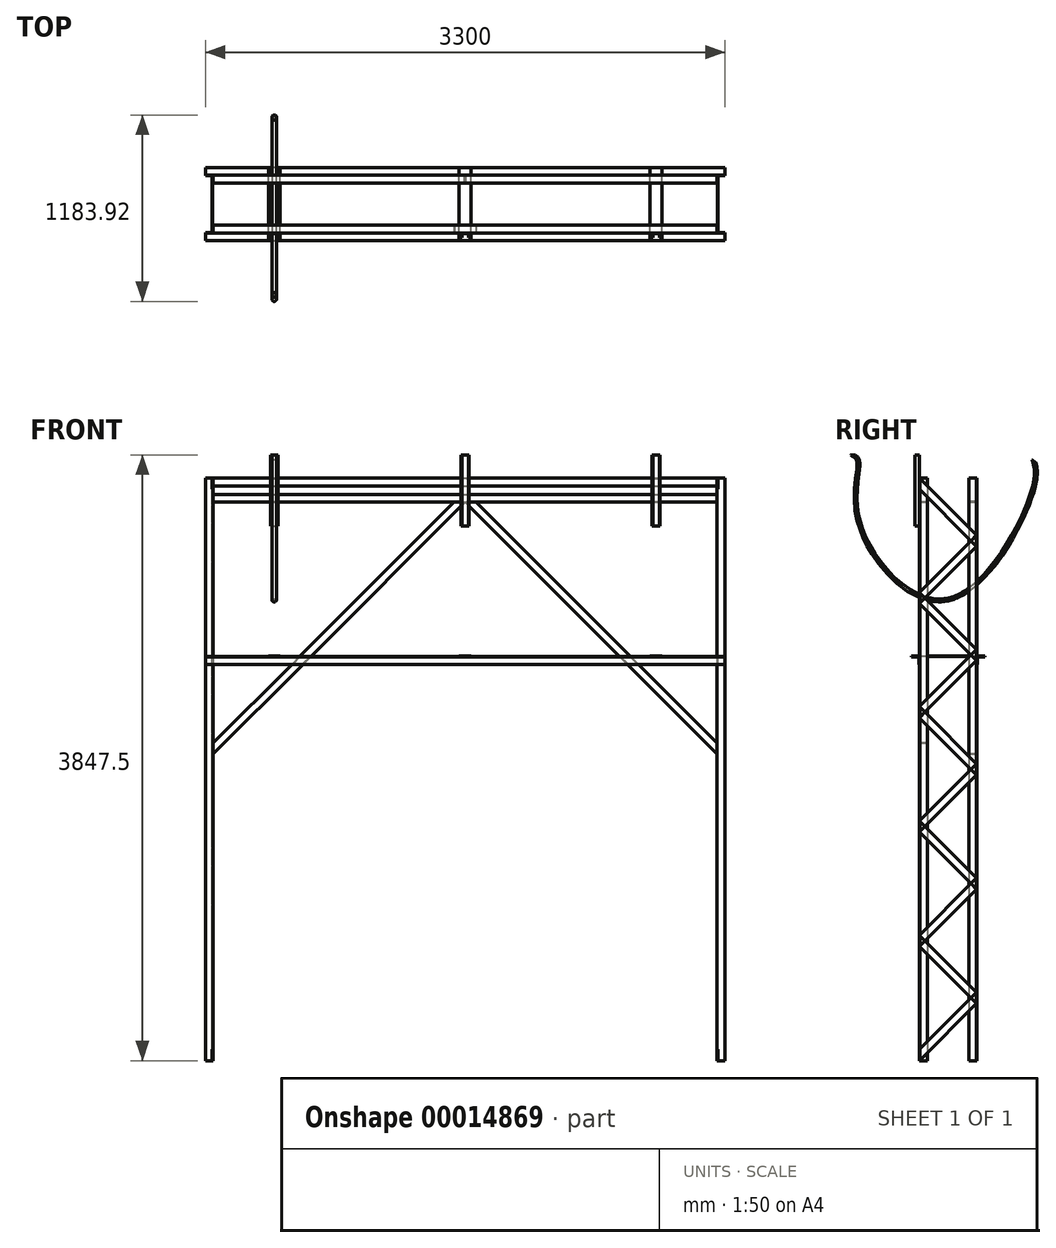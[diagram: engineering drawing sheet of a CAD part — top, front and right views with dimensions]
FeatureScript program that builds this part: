
annotation { "Feature Type Name" : "Feature", "Feature Type Description" : "" }
export const myFeature = defineFeature(function(context is Context, id is Id, definition is map)
    precondition{}
    {
        {
            var Q0;
            Q0=qCreatedBy(makeId("Top.planeOp"),FACE);
            var sketch = newSketch(context, id + "F0", { "sketchPlane" : qUnion([Q0])});
            skLineSegment(sketch, "E0", {"start": v(0, 0) * mm, "end": v(0, 50) * mm});
            skLineSegment(sketch, "E1", {"start": v(0, 50) * mm, "end": v(-3, 50) * mm});
            skLineSegment(sketch, "E2", {"start": v(-3, 50) * mm, "end": v(-3, 3) * mm});
            skLineSegment(sketch, "E3", {"start": v(-3, 3) * mm, "end": v(-50, 3) * mm});
            skLineSegment(sketch, "E4", {"start": v(-50, 3) * mm, "end": v(-50, 0) * mm});
            skLineSegment(sketch, "E5", {"start": v(-50, 0) * mm, "end": v(0, 0) * mm});
            skLineSegment(sketch, "E6", {"start": v(3200, 0) * mm, "end": v(3200, 50) * mm});
            skLineSegment(sketch, "E7", {"start": v(3200, 50) * mm, "end": v(3203, 50) * mm});
            skLineSegment(sketch, "E8", {"start": v(3203, 50) * mm, "end": v(3203, 3) * mm});
            skLineSegment(sketch, "E9", {"start": v(3203, 3) * mm, "end": v(3250, 3) * mm});
            skLineSegment(sketch, "E10", {"start": v(3250, 3) * mm, "end": v(3250, 0) * mm});
            skLineSegment(sketch, "E11", {"start": v(3250, 0) * mm, "end": v(3200, 0) * mm});
            skLineSegment(sketch, "E12", {"start": v(0, 316) * mm, "end": v(0, 366) * mm});
            skLineSegment(sketch, "E13", {"start": v(0, 366) * mm, "end": v(-50, 366) * mm});
            skLineSegment(sketch, "E14", {"start": v(-50, 366) * mm, "end": v(-50, 363) * mm});
            skLineSegment(sketch, "E15", {"start": v(-50, 363) * mm, "end": v(-3, 363) * mm});
            skLineSegment(sketch, "E16", {"start": v(-3, 363) * mm, "end": v(-3, 316) * mm});
            skLineSegment(sketch, "E17", {"start": v(-3, 316) * mm, "end": v(0, 316) * mm});
            skLineSegment(sketch, "E18", {"start": v(3200, 316) * mm, "end": v(3200, 366) * mm});
            skLineSegment(sketch, "E19", {"start": v(3200, 366) * mm, "end": v(3250, 366) * mm});
            skLineSegment(sketch, "E20", {"start": v(3250, 366) * mm, "end": v(3250, 363) * mm});
            skLineSegment(sketch, "E21", {"start": v(3250, 363) * mm, "end": v(3203, 363) * mm});
            skLineSegment(sketch, "E22", {"start": v(3203, 363) * mm, "end": v(3203, 316) * mm});
            skLineSegment(sketch, "E23", {"start": v(3203, 316) * mm, "end": v(3200, 316) * mm});
            skSolve(sketch);
        }
        {
            var Q0;
            Q0 = qSketchRegion(id + "F0", true);
            extrude(context, id + "F1", {"entities" : qUnion([Q0]), "depth" : 3700 * mm});
        }
        {
            var Q0;
            Q0=makeQuery(id+"F1.opExtrude","SWEPT_FACE",FACE,{"disambiguationData":[OSD([sQuery(id+"F0.wireOp",EDGE,"E22")])]});
            var sketch = newSketch(context, id + "F2", { "sketchPlane" : qUnion([Q0])});
            skLineSegment(sketch, "E24", {"start": v(0, 0) * mm, "end": v(363, 363) * mm});
            skLineSegment(sketch, "E25", {"start": v(363, 363) * mm, "end": v(0, 726) * mm});
            skLineSegment(sketch, "E26", {"start": v(0, 726) * mm, "end": v(363, 1089) * mm});
            skLineSegment(sketch, "E27", {"start": v(363, 1089) * mm, "end": v(0, 1452) * mm});
            skLineSegment(sketch, "E28", {"start": v(0, 1452) * mm, "end": v(363, 1815) * mm});
            skLineSegment(sketch, "E29", {"start": v(363, 1815) * mm, "end": v(0, 2178) * mm});
            skLineSegment(sketch, "E30", {"start": v(0, 2178) * mm, "end": v(363, 2541) * mm});
            skLineSegment(sketch, "E31", {"start": v(363, 2541) * mm, "end": v(0, 2904) * mm});
            skLineSegment(sketch, "E32", {"start": v(0, 2904) * mm, "end": v(363, 3267) * mm});
            skLineSegment(sketch, "E33", {"start": v(363, 3267) * mm, "end": v(0, 3630) * mm});
            skLineSegment(sketch, "E34", {"start": v(0, 0) * mm, "end": v(0, 70.7) * mm});
            skLineSegment(sketch, "E35", {"start": v(0, 70.71) * mm, "end": v(363, 433.7) * mm});
            skLineSegment(sketch, "E36", {"start": v(363, 433.7) * mm, "end": v(0, 796.7) * mm});
            skLineSegment(sketch, "E37", {"start": v(0, 796.7) * mm, "end": v(363, 1159.7) * mm});
            skLineSegment(sketch, "E38", {"start": v(363, 1159.7) * mm, "end": v(0, 1522.7) * mm});
            skLineSegment(sketch, "E39", {"start": v(0, 1522.7) * mm, "end": v(363, 1885.7) * mm});
            skLineSegment(sketch, "E40", {"start": v(363, 1885.7) * mm, "end": v(0, 2248.7) * mm});
            skLineSegment(sketch, "E41", {"start": v(0, 2248.7) * mm, "end": v(363, 2611.7) * mm});
            skLineSegment(sketch, "E42", {"start": v(363, 2611.7) * mm, "end": v(0, 2974.7) * mm});
            skLineSegment(sketch, "E43", {"start": v(0, 2974.7) * mm, "end": v(363, 3337.7) * mm});
            skLineSegment(sketch, "E44", {"start": v(363, 3337.7) * mm, "end": v(0, 3700.7) * mm});
            skLineSegment(sketch, "E45", {"start": v(0, 3700.7) * mm, "end": v(0, 3630) * mm});
            skLineSegment(sketch, "E46", {"start": v(0, 3601.1) * mm, "end": v(0, 3700.7) * mm});
            skLineSegment(sketch, "E47", {"start": v(0, 3630) * mm, "end": v(35.36, 3665.35) * mm});
            skLineSegment(sketch, "E48", {"start": v(35.35, 3665.35) * mm, "end": v(363, 3337.7) * mm});
            skLineSegment(sketch, "E49", {"start": v(327.64, 3302.35) * mm, "end": v(0, 3630) * mm});
            skLineSegment(sketch, "E50", {"start": v(0, 70.7) * mm, "end": v(35.35, 35.36) * mm});
            skLineSegment(sketch, "E51", {"start": v(35.35, 35.35) * mm, "end": v(363, 363) * mm});
            skLineSegment(sketch, "E52", {"start": v(363, 363) * mm, "end": v(327.64, 398.35) * mm});
            skLineSegment(sketch, "E53", {"start": v(327.64, 398.35) * mm, "end": v(0, 70.7) * mm});
            skSolve(sketch);
        }
        {
            var Q0;
            Q0 = qSketchRegion(id + "F2", true);
            extrude(context, id + "F3", {"entities" : qUnion([Q0]), "depth" : 3 * mm});
        }
        {
            var Q0;
            Q0=makeQuery(id+"F1.opExtrude","SWEPT_FACE",FACE,{"disambiguationData":[OSD([sQuery(id+"F0.wireOp",EDGE,"E16")])]});
            var sketch = newSketch(context, id + "F4", { "sketchPlane" : qUnion([Q0])});
            skLineSegment(sketch, "E54", {"start": v(0, 0) * mm, "end": v(-363, 363) * mm});
            skLineSegment(sketch, "E55", {"start": v(-363, 363) * mm, "end": v(0, 726) * mm});
            skLineSegment(sketch, "E56", {"start": v(0, 726) * mm, "end": v(-363, 1089) * mm});
            skLineSegment(sketch, "E57", {"start": v(-363, 1089) * mm, "end": v(0, 1452) * mm});
            skLineSegment(sketch, "E58", {"start": v(0, 1452) * mm, "end": v(-363, 1815) * mm});
            skLineSegment(sketch, "E59", {"start": v(-363, 1815) * mm, "end": v(0, 2178) * mm});
            skLineSegment(sketch, "E60", {"start": v(0, 2178) * mm, "end": v(-363, 2541) * mm});
            skLineSegment(sketch, "E61", {"start": v(-363, 2541) * mm, "end": v(0, 2904) * mm});
            skLineSegment(sketch, "E62", {"start": v(0, 2904) * mm, "end": v(-363, 3267) * mm});
            skLineSegment(sketch, "E63", {"start": v(-363, 3267) * mm, "end": v(0, 3630) * mm});
            skLineSegment(sketch, "E64", {"start": v(0, 3630) * mm, "end": v(0, 3700.7) * mm});
            skLineSegment(sketch, "E65", {"start": v(0, 0) * mm, "end": v(0, 70.7) * mm});
            skLineSegment(sketch, "E66", {"start": v(0, 70.71) * mm, "end": v(-363, 433.71) * mm});
            skLineSegment(sketch, "E67", {"start": v(-363, 433.71) * mm, "end": v(0, 796.71) * mm});
            skLineSegment(sketch, "E68", {"start": v(0, 796.71) * mm, "end": v(-363, 1159.71) * mm});
            skLineSegment(sketch, "E69", {"start": v(-363, 1159.71) * mm, "end": v(0, 1522.7) * mm});
            skLineSegment(sketch, "E70", {"start": v(0, 1522.7) * mm, "end": v(-363, 1885.7) * mm});
            skLineSegment(sketch, "E71", {"start": v(-363, 1885.7) * mm, "end": v(0, 2248.7) * mm});
            skLineSegment(sketch, "E72", {"start": v(0, 2248.7) * mm, "end": v(-363, 2611.7) * mm});
            skLineSegment(sketch, "E73", {"start": v(-363, 2611.7) * mm, "end": v(0, 2974.7) * mm});
            skLineSegment(sketch, "E74", {"start": v(0, 2974.7) * mm, "end": v(-363, 3337.7) * mm});
            skLineSegment(sketch, "E75", {"start": v(-363, 3337.7) * mm, "end": v(0, 3700.7) * mm});
            skSolve(sketch);
        }
        {
            var Q0;
            Q0 = qSketchRegion(id + "F4", true);
            extrude(context, id + "F5", {"entities" : qUnion([Q0]), "depth" : 3 * mm});
        }
        {
            var Q0;
            Q0=makeQuery(id+"F1.opExtrude","SWEPT_FACE",FACE,{"disambiguationData":[OSD([sQuery(id+"F0.wireOp",EDGE,"E18")])]});
            var sketch = newSketch(context, id + "F6", { "sketchPlane" : qUnion([Q0])});
            skLineSegment(sketch, "E76", {"start": v(-366, 3700) * mm, "end": v(-366, 3650) * mm});
            skLineSegment(sketch, "E77", {"start": v(-366, 3650) * mm, "end": v(-363, 3650) * mm});
            skLineSegment(sketch, "E78", {"start": v(-363, 3650) * mm, "end": v(-363, 3697) * mm});
            skLineSegment(sketch, "E79", {"start": v(-363, 3697) * mm, "end": v(-316, 3697) * mm});
            skLineSegment(sketch, "E80", {"start": v(-316, 3697) * mm, "end": v(-316, 3700) * mm});
            skLineSegment(sketch, "E81", {"start": v(-316, 3700) * mm, "end": v(-366, 3700) * mm});
            skLineSegment(sketch, "E82", {"start": v(-366, 3650) * mm, "end": v(-366, 3700) * mm});
            skLineSegment(sketch, "E83", {"start": v(0, 3650) * mm, "end": v(-3, 3650) * mm});
            skLineSegment(sketch, "E84", {"start": v(-3, 3650) * mm, "end": v(-3, 3697) * mm});
            skLineSegment(sketch, "E85", {"start": v(-3, 3697) * mm, "end": v(-50, 3697) * mm});
            skLineSegment(sketch, "E86", {"start": v(-50, 3697) * mm, "end": v(-50, 3700) * mm});
            skLineSegment(sketch, "E87", {"start": v(-50, 3700) * mm, "end": v(0, 3700) * mm});
            skLineSegment(sketch, "E88", {"start": v(0, 3700) * mm, "end": v(0, 3650) * mm});
            skLineSegment(sketch, "E89", {"start": v(-316, 3547.42) * mm, "end": v(-366, 3547.42) * mm});
            skLineSegment(sketch, "E90", {"start": v(-366, 3547.42) * mm, "end": v(-366, 3597.42) * mm});
            skLineSegment(sketch, "E91", {"start": v(-366, 3597.42) * mm, "end": v(-363, 3597.42) * mm});
            skLineSegment(sketch, "E92", {"start": v(-363, 3597.42) * mm, "end": v(-363, 3550.42) * mm});
            skLineSegment(sketch, "E93", {"start": v(-363, 3550.42) * mm, "end": v(-316, 3550.42) * mm});
            skLineSegment(sketch, "E94", {"start": v(-316, 3550.42) * mm, "end": v(-316, 3547.42) * mm});
            skLineSegment(sketch, "E95", {"start": v(-50, 3547.42) * mm, "end": v(0, 3547.42) * mm});
            skLineSegment(sketch, "E96", {"start": v(0, 3547.42) * mm, "end": v(0, 3597.42) * mm});
            skLineSegment(sketch, "E97", {"start": v(0, 3597.42) * mm, "end": v(-3, 3597.42) * mm});
            skLineSegment(sketch, "E98", {"start": v(-3, 3597.42) * mm, "end": v(-3, 3550.42) * mm});
            skLineSegment(sketch, "E99", {"start": v(-3, 3550.42) * mm, "end": v(-50, 3550.42) * mm});
            skLineSegment(sketch, "E100", {"start": v(-50, 3550.42) * mm, "end": v(-50, 3547.42) * mm});
            skSolve(sketch);
        }
        {
            var Q0;
            Q0=makeQuery(id+"F6.imprint","IMPRINT",FACE,{"disambiguationData":[TD([[makeQuery(id+"F6.imprint","IMPRINT",EDGE,{"derivedFrom":sQuery(id+"F6.wireOp",EDGE,"E89")}),-1.0]])]});
            var Q1;
            Q1=makeQuery(id+"F6.imprint","IMPRINT",FACE,{"disambiguationData":[TD([[makeQuery(id+"F6.imprint","IMPRINT",EDGE,{"derivedFrom":sQuery(id+"F6.wireOp",EDGE,"E77")}),1.0]])]});
            var Q2;
            Q2=makeQuery(id+"F6.imprint","IMPRINT",FACE,{"disambiguationData":[TD([[makeQuery(id+"F6.imprint","IMPRINT",EDGE,{"derivedFrom":sQuery(id+"F6.wireOp",EDGE,"E95")}),1.0]])]});
            var Q3;
            Q3=makeQuery(id+"F6.imprint","IMPRINT",FACE,{"disambiguationData":[TD([[makeQuery(id+"F6.imprint","IMPRINT",EDGE,{"derivedFrom":sQuery(id+"F6.wireOp",EDGE,"E83")}),-1.0]])]});
            extrude(context, id + "F7", {"entities" : qUnion([Q0, Q1, Q2, Q3]), "depth" : 3200 * mm});
        }
        {
            var Q0;
            Q0=makeQuery(id+"F7.opExtrude","SWEPT_FACE",FACE,{"disambiguationData":[OSD([sQuery(id+"F6.wireOp",EDGE,"E96")])]});
            var sketch = newSketch(context, id + "F8", { "sketchPlane" : qUnion([Q0])});
            skLineSegment(sketch, "E101", {"start": v(1600, 3547.42) * mm, "end": v(3200, 3547.42) * mm});
            skLineSegment(sketch, "E102", {"start": v(3200, 3547.42) * mm, "end": v(3200, 1947.42) * mm});
            skLineSegment(sketch, "E103", {"start": v(3200, 1947.42) * mm, "end": v(1600, 3547.42) * mm});
            skLineSegment(sketch, "E104", {"start": v(1600, 3547.42) * mm, "end": v(0, 3547.42) * mm});
            skLineSegment(sketch, "E105", {"start": v(0, 3547.42) * mm, "end": v(0, 1947.42) * mm});
            skLineSegment(sketch, "E106", {"start": v(0, 1947.42) * mm, "end": v(1600, 3547.42) * mm});
            skLineSegment(sketch, "E107", {"start": v(1600, 3547.42) * mm, "end": v(1529.29, 3547.42) * mm});
            skLineSegment(sketch, "E108", {"start": v(1529.29, 3547.42) * mm, "end": v(0, 2018.13) * mm});
            skLineSegment(sketch, "E109", {"start": v(0, 2018.13) * mm, "end": v(0, 1947.42) * mm});
            skLineSegment(sketch, "E110", {"start": v(1600, 3547.42) * mm, "end": v(1670.71, 3547.42) * mm});
            skLineSegment(sketch, "E111", {"start": v(1670.71, 3547.42) * mm, "end": v(3200, 2018.13) * mm});
            skLineSegment(sketch, "E112", {"start": v(3200, 2018.13) * mm, "end": v(3200, 1947.42) * mm});
            skSolve(sketch);
        }
        {
            var Q0;
            Q0=makeQuery(id+"F8.imprint","IMPRINT",FACE,{"disambiguationData":[TD([[makeQuery(id+"F8.imprint","IMPRINT",EDGE,{"derivedFrom":sQuery(id+"F8.wireOp",EDGE,"E103")}),-1.0]])]});
            var Q1;
            Q1=makeQuery(id+"F8.imprint","IMPRINT",FACE,{"disambiguationData":[TD([[makeQuery(id+"F8.imprint","IMPRINT",EDGE,{"derivedFrom":sQuery(id+"F8.wireOp",EDGE,"E106")}),1.0]])]});
            extrude(context, id + "F9", {"entities" : qUnion([Q0, Q1]), "oppositeDirection" : true, "depth" : 3 * mm});
        }
        {
            var Q0;
            Q0=makeQuery(id+"F9.opExtrude","CAP_FACE",FACE,{"disambiguationData":[OSD([sQuery(id+"F8.wireOp",EDGE,"E103"),sQuery(id+"F8.wireOp",EDGE,"E110"),sQuery(id+"F8.wireOp",EDGE,"E111"),sQuery(id+"F8.wireOp",EDGE,"E112")])],"isStart":false});
            var sketch = newSketch(context, id + "F10", { "sketchPlane" : qUnion([Q0])});
            skLineSegment(sketch, "E113", {"start": v(-1670.71, 3547.42) * mm, "end": v(-1668.59, 3545.3) * mm});
            skLineSegment(sketch, "E114", {"start": v(-1668.59, 3545.3) * mm, "end": v(-3200, 2013.89) * mm});
            skLineSegment(sketch, "E115", {"start": v(-3200, 2013.89) * mm, "end": v(-3200, 2018.13) * mm});
            skLineSegment(sketch, "E116", {"start": v(-3200, 2018.13) * mm, "end": v(-1670.7, 3547.42) * mm});
            skSolve(sketch);
        }
        {
            var Q0;
            Q0 = qSketchRegion(id + "F10", true);
            extrude(context, id + "F11", {"entities" : qUnion([Q0]), "depth" : 47 * mm});
        }
        {
            var Q0;
            Q0=makeQuery(id+"F9.opExtrude","CAP_FACE",FACE,{"disambiguationData":[OSD([sQuery(id+"F8.wireOp",EDGE,"E106"),sQuery(id+"F8.wireOp",EDGE,"E107"),sQuery(id+"F8.wireOp",EDGE,"E108"),sQuery(id+"F8.wireOp",EDGE,"E109")])],"isStart":false});
            var sketch = newSketch(context, id + "F12", { "sketchPlane" : qUnion([Q0])});
            skLineSegment(sketch, "E117", {"start": v(-1529.29, 3547.42) * mm, "end": v(-1531.41, 3545.3) * mm});
            skLineSegment(sketch, "E118", {"start": v(-1531.41, 3545.3) * mm, "end": v(0, 2013.89) * mm});
            skLineSegment(sketch, "E119", {"start": v(0, 2013.89) * mm, "end": v(0, 2018.13) * mm});
            skLineSegment(sketch, "E120", {"start": v(0, 2018.13) * mm, "end": v(-1529.29, 3547.42) * mm});
            skSolve(sketch);
        }
        {
            var Q0;
            Q0 = qSketchRegion(id + "F12", true);
            extrude(context, id + "F13", {"entities" : qUnion([Q0]), "depth" : 47 * mm});
        }
        {
            var Q0;
            Q0=makeQuery(id+"F7.opExtrude","SWEPT_FACE",FACE,{"disambiguationData":[OSD([sQuery(id+"F6.wireOp",EDGE,"E90")])]});
            var sketch = newSketch(context, id + "F14", { "sketchPlane" : qUnion([Q0])});
            skLineSegment(sketch, "E121", {"start": v(-1600, 3547.42) * mm, "end": v(0, 3547.42) * mm});
            skLineSegment(sketch, "E122", {"start": v(0, 3547.42) * mm, "end": v(0, 1947.42) * mm});
            skLineSegment(sketch, "E123", {"start": v(0, 1947.42) * mm, "end": v(-1600, 3547.42) * mm});
            skLineSegment(sketch, "E124", {"start": v(-1600, 3547.42) * mm, "end": v(-3200, 3547.42) * mm});
            skLineSegment(sketch, "E125", {"start": v(-3200, 3547.42) * mm, "end": v(-3200, 1947.42) * mm});
            skLineSegment(sketch, "E126", {"start": v(-3200, 1947.42) * mm, "end": v(-1600, 3547.42) * mm});
            skLineSegment(sketch, "E127", {"start": v(-1600, 3547.42) * mm, "end": v(-1529.3, 3547.42) * mm});
            skLineSegment(sketch, "E128", {"start": v(-1529.3, 3547.42) * mm, "end": v(0, 2018.13) * mm});
            skLineSegment(sketch, "E129", {"start": v(0, 2018.13) * mm, "end": v(0, 1947.42) * mm});
            skLineSegment(sketch, "E130", {"start": v(-1529.3, 3547.42) * mm, "end": v(-1600, 3547.42) * mm});
            skLineSegment(sketch, "E131", {"start": v(-1600, 3547.42) * mm, "end": v(-1670.71, 3547.42) * mm});
            skLineSegment(sketch, "E132", {"start": v(-1670.71, 3547.42) * mm, "end": v(-3200, 2018.13) * mm});
            skLineSegment(sketch, "E133", {"start": v(-3200, 2018.13) * mm, "end": v(-3200, 1947.42) * mm});
            skSolve(sketch);
        }
        {
            var Q0;
            Q0=makeQuery(id+"F14.imprint","IMPRINT",FACE,{"disambiguationData":[TD([[makeQuery(id+"F14.imprint","IMPRINT",EDGE,{"derivedFrom":sQuery(id+"F14.wireOp",EDGE,"E123")}),-1.0]])]});
            var Q1;
            Q1=makeQuery(id+"F14.imprint","IMPRINT",FACE,{"disambiguationData":[TD([[makeQuery(id+"F14.imprint","IMPRINT",EDGE,{"derivedFrom":sQuery(id+"F14.wireOp",EDGE,"E126")}),1.0]])]});
            extrude(context, id + "F15", {"entities" : qUnion([Q0, Q1]), "oppositeDirection" : true, "depth" : 3 * mm});
        }
        {
            var Q0;
            Q0=makeQuery(id+"F15.opExtrude","CAP_FACE",FACE,{"disambiguationData":[OSD([sQuery(id+"F14.wireOp",EDGE,"E123"),sQuery(id+"F14.wireOp",EDGE,"E128"),sQuery(id+"F14.wireOp",EDGE,"E129"),sQuery(id+"F14.wireOp",EDGE,"E130")])],"isStart":false});
            var sketch = newSketch(context, id + "F16", { "sketchPlane" : qUnion([Q0])});
            skLineSegment(sketch, "E134", {"start": v(1600, 3547.42) * mm, "end": v(1595.76, 3547.42) * mm});
            skLineSegment(sketch, "E135", {"start": v(1595.76, 3547.42) * mm, "end": v(0, 1951.66) * mm});
            skLineSegment(sketch, "E136", {"start": v(0, 1951.66) * mm, "end": v(0, 1947.42) * mm});
            skLineSegment(sketch, "E137", {"start": v(0, 1947.42) * mm, "end": v(1600, 3547.42) * mm});
            skSolve(sketch);
        }
        {
            var Q0;
            Q0 = qSketchRegion(id + "F16", true);
            extrude(context, id + "F17", {"entities" : qUnion([Q0]), "depth" : 47 * mm});
        }
        {
            var Q0;
            Q0=makeQuery(id+"F15.opExtrude","CAP_FACE",FACE,{"disambiguationData":[OSD([sQuery(id+"F14.wireOp",EDGE,"E126"),sQuery(id+"F14.wireOp",EDGE,"E131"),sQuery(id+"F14.wireOp",EDGE,"E132"),sQuery(id+"F14.wireOp",EDGE,"E133")])],"isStart":false});
            var sketch = newSketch(context, id + "F18", { "sketchPlane" : qUnion([Q0])});
            skLineSegment(sketch, "E138", {"start": v(1600, 3547.42) * mm, "end": v(1604.24, 3547.42) * mm});
            skLineSegment(sketch, "E139", {"start": v(1604.24, 3547.42) * mm, "end": v(3200, 1951.66) * mm});
            skLineSegment(sketch, "E140", {"start": v(3200, 1951.66) * mm, "end": v(3200, 1947.42) * mm});
            skLineSegment(sketch, "E141", {"start": v(3200, 1947.42) * mm, "end": v(1600, 3547.42) * mm});
            skSolve(sketch);
        }
        {
            var Q0;
            Q0 = qSketchRegion(id + "F18", true);
            extrude(context, id + "F19", {"entities" : qUnion([Q0]), "depth" : 47 * mm});
        }
        {
            var Q0;
            Q0=makeQuery(id+"F15.opExtrude","CAP_FACE",FACE,{"disambiguationData":[OSD([sQuery(id+"F14.wireOp",EDGE,"E126"),sQuery(id+"F14.wireOp",EDGE,"E131"),sQuery(id+"F14.wireOp",EDGE,"E132"),sQuery(id+"F14.wireOp",EDGE,"E133")])],"isStart":true});
            var sketch = newSketch(context, id + "F20", { "sketchPlane" : qUnion([Q0])});
            skLineSegment(sketch, "E142.bottom", {"start": v(-3250, 2567.42) * mm, "end": v(50, 2567.42) * mm});
            skLineSegment(sketch, "E142.top", {"start": v(-3250, 2517.42) * mm, "end": v(50, 2517.42) * mm});
            skLineSegment(sketch, "E142.left", {"start": v(-3250, 2567.42) * mm, "end": v(-3250, 2517.42) * mm});
            skLineSegment(sketch, "E142.right", {"start": v(50, 2567.42) * mm, "end": v(50, 2517.42) * mm});
            skSolve(sketch);
        }
        {
            var Q0;
            Q0 = qSketchRegion(id + "F20", true);
            extrude(context, id + "F21", {"entities" : qUnion([Q0]), "depth" : 3 * mm});
        }
        {
            var Q0;
            Q0=makeQuery(id+"F21.opExtrude","CAP_FACE",FACE,{"disambiguationData":[OSD([sQuery(id+"F20.wireOp",EDGE,"E142.bottom"),sQuery(id+"F20.wireOp",EDGE,"E142.top"),sQuery(id+"F20.wireOp",EDGE,"E142.left"),sQuery(id+"F20.wireOp",EDGE,"E142.right")])],"isStart":false});
            var sketch = newSketch(context, id + "F22", { "sketchPlane" : qUnion([Q0])});
            skLineSegment(sketch, "E143.bottom", {"start": v(50, 2567.42) * mm, "end": v(-3250, 2567.42) * mm});
            skLineSegment(sketch, "E143.top", {"start": v(50, 2564.42) * mm, "end": v(-3250, 2564.42) * mm});
            skLineSegment(sketch, "E143.left", {"start": v(50, 2567.42) * mm, "end": v(50, 2564.42) * mm});
            skLineSegment(sketch, "E143.right", {"start": v(-3250, 2567.42) * mm, "end": v(-3250, 2564.42) * mm});
            skSolve(sketch);
        }
        {
            var Q0;
            Q0 = qSketchRegion(id + "F22", true);
            extrude(context, id + "F23", {"entities" : qUnion([Q0]), "operationType" : NewBodyOperationType.ADD, "depth" : 47 * mm});
        }
        {
            var Q0;
            Q0=makeQuery(id+"F9.opExtrude","CAP_FACE",FACE,{"disambiguationData":[OSD([sQuery(id+"F8.wireOp",EDGE,"E106"),sQuery(id+"F8.wireOp",EDGE,"E107"),sQuery(id+"F8.wireOp",EDGE,"E108"),sQuery(id+"F8.wireOp",EDGE,"E109")])],"isStart":true});
            var sketch = newSketch(context, id + "F24", { "sketchPlane" : qUnion([Q0])});
            skSolve(sketch);
        }
        {
            var Q0;
            Q0=makeQuery(id+"F24.imprint","IMPRINT",FACE,{"disambiguationData":[TD([[makeQuery(id+"F24.imprint","IMPRINT",EDGE,{"derivedFrom":makeQuery(id+"F9.opExtrude","CAP_EDGE",EDGE,{"disambiguationData":[OSD([sQuery(id+"F8.wireOp",EDGE,"E106")])],"isStart":true})}),1.0]])]});
            var sketch = newSketch(context, id + "F25", { "sketchPlane" : qUnion([Q0])});
            skLineSegment(sketch, "E144.bottom", {"start": v(-50, 2567.42) * mm, "end": v(3250, 2567.42) * mm});
            skLineSegment(sketch, "E144.top", {"start": v(-50, 2517.42) * mm, "end": v(3250, 2517.42) * mm});
            skLineSegment(sketch, "E144.left", {"start": v(-50, 2567.42) * mm, "end": v(-50, 2517.42) * mm});
            skLineSegment(sketch, "E144.right", {"start": v(3250, 2567.42) * mm, "end": v(3250, 2517.42) * mm});
            skSolve(sketch);
        }
        {
            var Q0;
            Q0 = qSketchRegion(id + "F25", true);
            extrude(context, id + "F26", {"entities" : qUnion([Q0]), "depth" : 3 * mm});
        }
        {
            var Q0;
            Q0=makeQuery(id+"F26.opExtrude","CAP_FACE",FACE,{"disambiguationData":[OSD([sQuery(id+"F25.wireOp",EDGE,"E144.bottom"),sQuery(id+"F25.wireOp",EDGE,"E144.top"),sQuery(id+"F25.wireOp",EDGE,"E144.left"),sQuery(id+"F25.wireOp",EDGE,"E144.right")])],"isStart":false});
            var sketch = newSketch(context, id + "F27", { "sketchPlane" : qUnion([Q0])});
            skLineSegment(sketch, "E145.bottom", {"start": v(-50, 2567.42) * mm, "end": v(3250, 2567.42) * mm});
            skLineSegment(sketch, "E145.top", {"start": v(-50, 2564.42) * mm, "end": v(3250, 2564.42) * mm});
            skLineSegment(sketch, "E145.left", {"start": v(-50, 2567.42) * mm, "end": v(-50, 2564.42) * mm});
            skLineSegment(sketch, "E145.right", {"start": v(3250, 2567.42) * mm, "end": v(3250, 2564.42) * mm});
            skSolve(sketch);
        }
        {
            var Q0;
            Q0=makeQuery(id+"F27.imprint","IMPRINT",FACE,{"disambiguationData":[TD([[makeQuery(id+"F27.imprint","IMPRINT",EDGE,{"derivedFrom":sQuery(id+"F27.wireOp",EDGE,"E145.bottom")}),-1.0]])]});
            extrude(context, id + "F28", {"entities" : qUnion([Q0]), "operationType" : NewBodyOperationType.ADD, "depth" : 47 * mm});
        }
        {
            var Q0;
            Q0=makeQuery(id+"F28.boolean.opBoolean","MERGE",FACE,{"derivedFrom":[makeQuery(id+"F26.opExtrude","SWEPT_FACE",FACE,{"disambiguationData":[OSD([sQuery(id+"F25.wireOp",EDGE,"E144.bottom")])]}),makeQuery(id+"F28.opExtrude","SWEPT_FACE",FACE,{"disambiguationData":[OSD([sQuery(id+"F27.wireOp",EDGE,"E145.bottom")])]})]});
            var sketch = newSketch(context, id + "F29", { "sketchPlane" : qUnion([Q0])});
            skLineSegment(sketch, "E146.bottom", {"start": v(1600, -50) * mm, "end": v(1637.5, -50) * mm});
            skLineSegment(sketch, "E146.top", {"start": v(1600, 416) * mm, "end": v(1637.5, 416) * mm});
            skLineSegment(sketch, "E146.right", {"start": v(1637.5, -50) * mm, "end": v(1637.5, 416) * mm});
            skLineSegment(sketch, "E147.bottom", {"start": v(1600, -50) * mm, "end": v(1562.5, -50) * mm});
            skLineSegment(sketch, "E147.top", {"start": v(1600, 416) * mm, "end": v(1562.5, 416) * mm});
            skLineSegment(sketch, "E147.right", {"start": v(1562.5, -50) * mm, "end": v(1562.5, 416) * mm});
            skLineSegment(sketch, "E148.bottom", {"start": v(2775, -50) * mm, "end": v(2850, -50) * mm});
            skLineSegment(sketch, "E148.top", {"start": v(2775, 416) * mm, "end": v(2850, 416) * mm});
            skLineSegment(sketch, "E148.left", {"start": v(2775, -50) * mm, "end": v(2775, 416) * mm});
            skLineSegment(sketch, "E148.right", {"start": v(2850, -50) * mm, "end": v(2850, 416) * mm});
            skLineSegment(sketch, "E149.bottom", {"start": v(425, -50) * mm, "end": v(350, -50) * mm});
            skLineSegment(sketch, "E149.top", {"start": v(425, 416) * mm, "end": v(350, 416) * mm});
            skLineSegment(sketch, "E149.left", {"start": v(425, -50) * mm, "end": v(425, 416) * mm});
            skLineSegment(sketch, "E149.right", {"start": v(350, -50) * mm, "end": v(350, 416) * mm});
            skSolve(sketch);
        }
        {
            var Q0;
            Q0 = qSketchRegion(id + "F29", true);
            extrude(context, id + "F30", {"entities" : qUnion([Q0]), "depth" : 4 * mm});
        }
        {
            var Q0;
            Q0=makeQuery(id+"F7.opExtrude","SWEPT_FACE",FACE,{"disambiguationData":[OSD([sQuery(id+"F6.wireOp",EDGE,"E88")])]});
            var sketch = newSketch(context, id + "F31", { "sketchPlane" : qUnion([Q0])});
            skLineSegment(sketch, "E150.bottom", {"start": v(362.5, 3397.42) * mm, "end": v(412.5, 3397.42) * mm});
            skLineSegment(sketch, "E150.top", {"start": v(362.5, 3847.42) * mm, "end": v(412.5, 3847.42) * mm});
            skLineSegment(sketch, "E150.left", {"start": v(362.5, 3397.42) * mm, "end": v(362.5, 3847.42) * mm});
            skLineSegment(sketch, "E150.right", {"start": v(412.5, 3397.42) * mm, "end": v(412.5, 3847.42) * mm});
            skLineSegment(sketch, "E151.top", {"start": v(1600, 3397.42) * mm, "end": v(1625, 3397.42) * mm});
            skLineSegment(sketch, "E151.right", {"start": v(1625, 3625) * mm, "end": v(1625, 3397.42) * mm});
            skLineSegment(sketch, "E152.bottom", {"start": v(1625, 3397.42) * mm, "end": v(1575, 3397.42) * mm});
            skLineSegment(sketch, "E152.top", {"start": v(1625, 3847.42) * mm, "end": v(1575, 3847.42) * mm});
            skLineSegment(sketch, "E152.left", {"start": v(1625, 3397.42) * mm, "end": v(1625, 3847.42) * mm});
            skLineSegment(sketch, "E152.right", {"start": v(1575, 3397.42) * mm, "end": v(1575, 3847.42) * mm});
            skLineSegment(sketch, "E153.bottom", {"start": v(2787.5, 3847.42) * mm, "end": v(2837.5, 3847.42) * mm});
            skLineSegment(sketch, "E153.top", {"start": v(2787.5, 3397.42) * mm, "end": v(2837.5, 3397.42) * mm});
            skLineSegment(sketch, "E153.left", {"start": v(2787.5, 3847.42) * mm, "end": v(2787.5, 3397.42) * mm});
            skLineSegment(sketch, "E153.right", {"start": v(2837.5, 3847.42) * mm, "end": v(2837.5, 3397.42) * mm});
            skPoint(sketch, "E151.bottom.start.orphan", {"position": v(1600, 3700) * mm});
            skSolve(sketch);
        }
        {
            var Q0;
            {var subQ5=sQuery(id+"F31.wireOp",EDGE,"E150.top");Q0=makeQuery(id+"F31.imprint","IMPRINT",FACE,{"disambiguationData":[TD([[makeQuery(id+"F31.imprint","IMPRINT",EDGE,{"derivedFrom":subQ5}),-1.0]])]});}
            var Q1;
            {var subQ0=sQuery(id+"F6.wireOp",EDGE,"E88");var subQ1=makeQuery(id+"F7.opExtrude","SWEPT_EDGE",EDGE,{"disambiguationData":[OSD([sQuery(id+"F6.wireOp",EDGE,"E83"),subQ0])]});var subQ4=sQuery(id+"F31.wireOp",EDGE,"E150.left");var subQ5=makeQuery(id+"F31.imprint","INTERSECT",VERTEX,{"derivedFrom":[subQ1,subQ4]});Q1=makeQuery(id+"F31.imprint","IMPRINT",FACE,{"disambiguationData":[TD([[makeQuery(id+"F31.imprint","IMPRINT",EDGE,{"disambiguationData":[TD([[subQ5,-1.0]])],"derivedFrom":subQ4}),-1.0]])]});}
            var Q2;
            {var subQ5=sQuery(id+"F31.wireOp",EDGE,"E150.bottom");Q2=makeQuery(id+"F31.imprint","IMPRINT",FACE,{"disambiguationData":[TD([[makeQuery(id+"F31.imprint","IMPRINT",EDGE,{"derivedFrom":subQ5}),1.0]])]});}
            var Q3;
            {var subQ3=sQuery(id+"F31.wireOp",EDGE,"E152.left");var subQ5=sQuery(id+"F31.wireOp",EDGE,"E152.bottom");var subQ7=makeQuery(id+"F31.imprint","INTERSECT",VERTEX,{"derivedFrom":[subQ5,subQ3]});Q3=makeQuery(id+"F31.imprint","IMPRINT",FACE,{"disambiguationData":[TD([[makeQuery(id+"F31.imprint","IMPRINT",EDGE,{"disambiguationData":[TD([[subQ7,-1.0]])],"derivedFrom":subQ5}),-1.0]])]});}
            var Q4;
            {var subQ0=sQuery(id+"F6.wireOp",EDGE,"E88");var subQ4=sQuery(id+"F31.wireOp",EDGE,"E152.left");var subQ6=makeQuery(id+"F7.opExtrude","SWEPT_EDGE",EDGE,{"disambiguationData":[OSD([sQuery(id+"F6.wireOp",EDGE,"E83"),subQ0])]});var subQ8=makeQuery(id+"F31.imprint","INTERSECT",VERTEX,{"derivedFrom":[subQ6,subQ4]});Q4=makeQuery(id+"F31.imprint","IMPRINT",FACE,{"disambiguationData":[TD([[makeQuery(id+"F31.imprint","IMPRINT",EDGE,{"disambiguationData":[TD([[subQ8,-1.0]])],"derivedFrom":subQ4}),1.0]])]});}
            var Q5;
            {var subQ5=sQuery(id+"F31.wireOp",EDGE,"E152.top");Q5=makeQuery(id+"F31.imprint","IMPRINT",FACE,{"disambiguationData":[TD([[makeQuery(id+"F31.imprint","IMPRINT",EDGE,{"derivedFrom":subQ5}),1.0]])]});}
            var Q6;
            {var subQ5=sQuery(id+"F31.wireOp",EDGE,"E153.top");Q6=makeQuery(id+"F31.imprint","IMPRINT",FACE,{"disambiguationData":[TD([[makeQuery(id+"F31.imprint","IMPRINT",EDGE,{"derivedFrom":subQ5}),1.0]])]});}
            var Q7;
            {var subQ0=sQuery(id+"F6.wireOp",EDGE,"E88");var subQ1=makeQuery(id+"F7.opExtrude","SWEPT_EDGE",EDGE,{"disambiguationData":[OSD([sQuery(id+"F6.wireOp",EDGE,"E87"),subQ0])]});var subQ4=sQuery(id+"F31.wireOp",EDGE,"E153.left");var subQ5=makeQuery(id+"F31.imprint","INTERSECT",VERTEX,{"derivedFrom":[subQ1,subQ4]});Q7=makeQuery(id+"F31.imprint","IMPRINT",FACE,{"disambiguationData":[TD([[makeQuery(id+"F31.imprint","IMPRINT",EDGE,{"disambiguationData":[TD([[subQ5,-1.0]])],"derivedFrom":subQ4}),1.0]])]});}
            var Q8;
            {var subQ5=sQuery(id+"F31.wireOp",EDGE,"E153.bottom");Q8=makeQuery(id+"F31.imprint","IMPRINT",FACE,{"disambiguationData":[TD([[makeQuery(id+"F31.imprint","IMPRINT",EDGE,{"derivedFrom":subQ5}),-1.0]])]});}
            extrude(context, id + "F32", {"entities" : qUnion([Q0, Q1, Q2, Q3, Q4, Q5, Q6, Q7, Q8]), "depth" : 4 * mm});
        }
        {
            var Q0;
            Q0=makeQuery(id+"F32.opExtrude","CAP_FACE",FACE,{"disambiguationData":[OSD([sQuery(id+"F31.wireOp",EDGE,"E150.bottom"),sQuery(id+"F31.wireOp",EDGE,"E150.top"),sQuery(id+"F31.wireOp",EDGE,"E150.left"),sQuery(id+"F31.wireOp",EDGE,"E150.right")])],"isStart":false});
            var sketch = newSketch(context, id + "F33", { "sketchPlane" : qUnion([Q0])});
            skLineSegment(sketch, "E154.bottom", {"start": v(362.5, 3847.42) * mm, "end": v(366.5, 3847.42) * mm});
            skLineSegment(sketch, "E154.top", {"start": v(362.5, 3397.42) * mm, "end": v(366.5, 3397.42) * mm});
            skLineSegment(sketch, "E154.left", {"start": v(362.5, 3847.42) * mm, "end": v(362.5, 3397.42) * mm});
            skLineSegment(sketch, "E154.right", {"start": v(366.5, 3847.42) * mm, "end": v(366.5, 3397.42) * mm});
            skLineSegment(sketch, "E155.bottom", {"start": v(412.5, 3397.42) * mm, "end": v(408.5, 3397.42) * mm});
            skLineSegment(sketch, "E155.top", {"start": v(412.5, 3847.42) * mm, "end": v(408.5, 3847.42) * mm});
            skLineSegment(sketch, "E155.left", {"start": v(412.5, 3397.42) * mm, "end": v(412.5, 3847.42) * mm});
            skLineSegment(sketch, "E155.right", {"start": v(408.5, 3397.42) * mm, "end": v(408.5, 3847.42) * mm});
            skSolve(sketch);
        }
        {
            var Q0;
            Q0 = qSketchRegion(id + "F33", true);
            extrude(context, id + "F34", {"entities" : qUnion([Q0]), "operationType" : NewBodyOperationType.ADD, "depth" : 25 * mm});
        }
        {
            var Q0;
            Q0=makeQuery(id+"F32.opExtrude","CAP_FACE",FACE,{"disambiguationData":[OSD([sQuery(id+"F31.wireOp",EDGE,"E152.bottom"),sQuery(id+"F31.wireOp",EDGE,"E152.top"),sQuery(id+"F31.wireOp",EDGE,"E152.left"),sQuery(id+"F31.wireOp",EDGE,"E152.right")])],"isStart":false});
            var sketch = newSketch(context, id + "F35", { "sketchPlane" : qUnion([Q0])});
            skLineSegment(sketch, "E156.bottom", {"start": v(1625, 3847.42) * mm, "end": v(1621, 3847.42) * mm});
            skLineSegment(sketch, "E156.top", {"start": v(1625, 3397.42) * mm, "end": v(1621, 3397.42) * mm});
            skLineSegment(sketch, "E156.left", {"start": v(1625, 3847.42) * mm, "end": v(1625, 3397.42) * mm});
            skLineSegment(sketch, "E156.right", {"start": v(1621, 3847.42) * mm, "end": v(1621, 3397.42) * mm});
            skLineSegment(sketch, "E157.bottom", {"start": v(1575, 3397.42) * mm, "end": v(1579, 3397.42) * mm});
            skLineSegment(sketch, "E157.top", {"start": v(1575, 3847.42) * mm, "end": v(1579, 3847.42) * mm});
            skLineSegment(sketch, "E157.left", {"start": v(1575, 3397.42) * mm, "end": v(1575, 3847.42) * mm});
            skLineSegment(sketch, "E157.right", {"start": v(1579, 3397.42) * mm, "end": v(1579, 3847.42) * mm});
            skSolve(sketch);
        }
        {
            var Q0;
            Q0 = qSketchRegion(id + "F35", true);
            extrude(context, id + "F36", {"entities" : qUnion([Q0]), "operationType" : NewBodyOperationType.ADD, "depth" : 25 * mm});
        }
        {
            var Q0;
            Q0=makeQuery(id+"F32.opExtrude","CAP_FACE",FACE,{"disambiguationData":[OSD([sQuery(id+"F31.wireOp",EDGE,"E153.bottom"),sQuery(id+"F31.wireOp",EDGE,"E153.top"),sQuery(id+"F31.wireOp",EDGE,"E153.left"),sQuery(id+"F31.wireOp",EDGE,"E153.right")])],"isStart":false});
            var sketch = newSketch(context, id + "F37", { "sketchPlane" : qUnion([Q0])});
            skLineSegment(sketch, "E158.bottom", {"start": v(2837.5, 3847.42) * mm, "end": v(2833.5, 3847.42) * mm});
            skLineSegment(sketch, "E158.top", {"start": v(2837.5, 3397.42) * mm, "end": v(2833.5, 3397.42) * mm});
            skLineSegment(sketch, "E158.left", {"start": v(2837.5, 3847.42) * mm, "end": v(2837.5, 3397.42) * mm});
            skLineSegment(sketch, "E158.right", {"start": v(2833.5, 3847.42) * mm, "end": v(2833.5, 3397.42) * mm});
            skLineSegment(sketch, "E159.bottom", {"start": v(2787.5, 3397.42) * mm, "end": v(2791.5, 3397.42) * mm});
            skLineSegment(sketch, "E159.top", {"start": v(2787.5, 3847.42) * mm, "end": v(2791.5, 3847.42) * mm});
            skLineSegment(sketch, "E159.left", {"start": v(2787.5, 3397.42) * mm, "end": v(2787.5, 3847.42) * mm});
            skLineSegment(sketch, "E159.right", {"start": v(2791.5, 3397.42) * mm, "end": v(2791.5, 3847.42) * mm});
            skSolve(sketch);
        }
        {
            var Q0;
            Q0 = qSketchRegion(id + "F37", true);
            extrude(context, id + "F38", {"entities" : qUnion([Q0]), "operationType" : NewBodyOperationType.ADD, "depth" : 25 * mm});
        }
        {
            var Q0;
            Q0=makeQuery(id+"F34.boolean.opBoolean","MERGE",FACE,{"derivedFrom":[makeQuery(id+"F32.opExtrude","SWEPT_FACE",FACE,{"disambiguationData":[OSD([sQuery(id+"F31.wireOp",EDGE,"E150.left")])]}),makeQuery(id+"F34.opExtrude","SWEPT_FACE",FACE,{"disambiguationData":[OSD([sQuery(id+"F33.wireOp",EDGE,"E154.left")])]})]});
            var sketch = newSketch(context, id + "F39", { "sketchPlane" : qUnion([Q0])});
            skFitSpline(sketch, "E160", {"points": [v(421.05, 3847.42) * mm, v(389, 3807.8) * mm, v(389, 3439.33) * mm, v(-178.2, 2928.78) * mm, v(-733.41, 3674.14) * mm, v(-727.28, 3807.8) * mm], "startDerivative": vector(-511.31, -425.46) * mm, "endDerivative": vector(152.77, 626.07) * mm});
            skSolve(sketch);
        }
        {
            var Q0;
            Q0=qCreatedBy(makeId("Top.planeOp"),FACE);
            cPlane(context, id + "F40", {"entities" : qUnion([Q0]), "cplaneType" : CPlaneType.OFFSET, "offset" : 3847.5 * mm, "width" : 150 * mm, "height" : 150 * mm});
        }
        {
            var Q0;
            Q0=qCreatedBy(id+"F40.planeOp",FACE);
            var sketch = newSketch(context, id + "F41", { "sketchPlane" : qUnion([Q0])});
            skCircle(sketch, "E161", {"center": v(387.5, -420.98) * mm, "radius": 14 * mm});
            skLineSegment(sketch, "E162", {"start": v(409.1, -28.96) * mm, "end": v(366.9, -28.96) * mm});
            skSolve(sketch);
        }
        {
            var Q0;
            Q0=makeQuery(id+"F41.imprint","IMPRINT",FACE,{"disambiguationData":[TD([[makeQuery(id+"F41.imprint","IMPRINT",EDGE,{"derivedFrom":sQuery(id+"F41.wireOp",EDGE,"E161")}),1.0]])]});
            var Q1;
            Q1=sQuery(id+"F39.wireOp",EDGE,"E160");
            sweep(context, id + "F42", {"profiles" : qUnion([Q0]), "path" : qUnion([Q1])});
        }
    });
